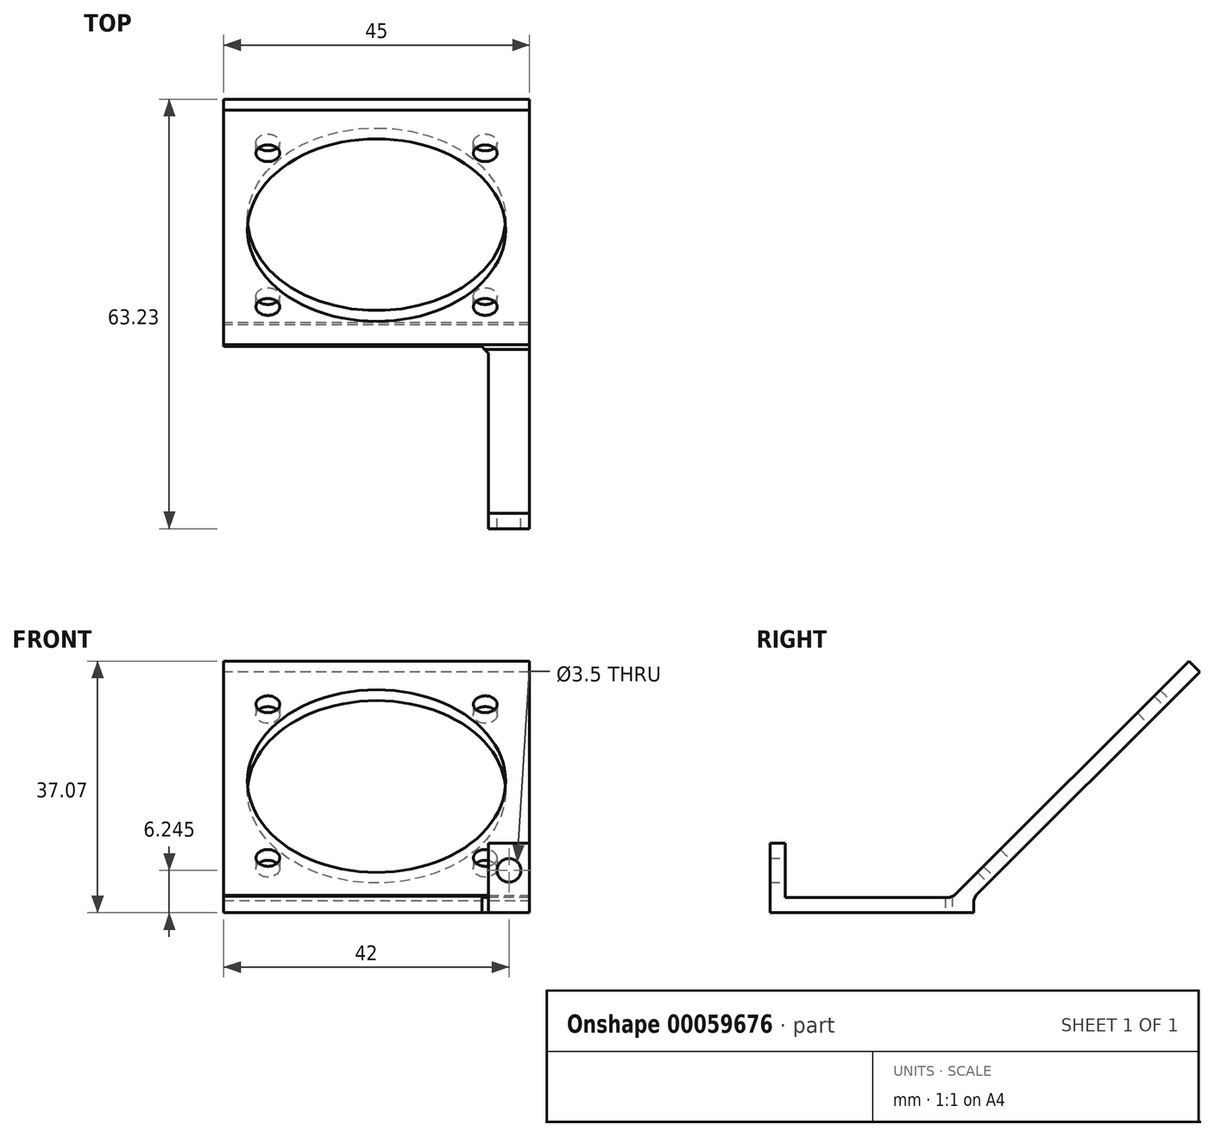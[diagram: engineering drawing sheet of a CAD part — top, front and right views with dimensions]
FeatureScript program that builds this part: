
annotation { "Feature Type Name" : "Feature", "Feature Type Description" : "" }
export const myFeature = defineFeature(function(context is Context, id is Id, definition is map)
    precondition{}
    {
        {
            var Q0;
            Q0=qCreatedBy(makeId("Right.planeOp"),FACE);
            var sketch = newSketch(context, id + "F0", { "sketchPlane" : qUnion([Q0])});
            skLineSegment(sketch, "E0.rect.bottom", {"start": v(15, 1.13) * mm, "end": v(-15, 1.12) * mm});
            skLineSegment(sketch, "E0.rect.top", {"start": v(15, -1.12) * mm, "end": v(-15, -1.13) * mm});
            skLineSegment(sketch, "E0.rect.left", {"start": v(15, 1.13) * mm, "end": v(15, -1.12) * mm});
            skLineSegment(sketch, "E0.rect.right", {"start": v(-15, 1.12) * mm, "end": v(-15, -1.13) * mm});
            skPoint(sketch, "E0.rect.middle", {"position": v(0, 0) * mm});
            skLineSegment(sketch, "E1", {"start": v(15, 1.13) * mm, "end": v(48.23, 34.36) * mm});
            skLineSegment(sketch, "E2.0", {"start": v(11.82, 1.13) * mm, "end": v(46.64, 35.95) * mm});
            skLineSegment(sketch, "E3", {"start": v(48.23, 34.36) * mm, "end": v(46.64, 35.95) * mm});
            skLineSegment(sketch, "E4.bottom", {"start": v(-15, 1.12) * mm, "end": v(-12.75, 1.12) * mm});
            skLineSegment(sketch, "E4.top", {"start": v(-15, 9.12) * mm, "end": v(-12.75, 9.12) * mm});
            skLineSegment(sketch, "E4.left", {"start": v(-15, 1.12) * mm, "end": v(-15, 9.12) * mm});
            skLineSegment(sketch, "E4.right", {"start": v(-12.75, 1.12) * mm, "end": v(-12.75, 9.12) * mm});
            skSolve(sketch);
        }
        {
            var Q0;
            Q0 = qSketchRegion(id + "F0", true);
            extrude(context, id + "F1", {"entities" : qUnion([Q0]), "depth" : 45 * mm});
        }
        {
            var Q0;
            Q0=makeQuery(id+"F1.opExtrude","SWEPT_FACE",FACE,{"disambiguationData":[OSD([sQuery(id+"F0.wireOp",EDGE,"E1")])]});
            var sketch = newSketch(context, id + "F2", { "sketchPlane" : qUnion([Q0])});
            skCircle(sketch, "E5", {"center": v(-22.5, 33.4) * mm, "radius": 19 * mm});
            skPoint(sketch, "E5.centerSnap0", {"position": v(-22.5, 58.4) * mm});
            skCircle(sketch, "E6", {"center": v(-6.5, 17.4) * mm, "radius": 1.75 * mm});
            skLineSegment(sketch, "E7", {"start": v(-22.5, 11.4) * mm, "end": v(-22.5, 58.4) * mm, "construction": true});
            skCircle(sketch, "E8.MirrorC", {"center": v(-38.5, 17.4) * mm, "radius": 1.75 * mm});
            skLineSegment(sketch, "E9", {"start": v(0, 33.4) * mm, "end": v(-45, 33.4) * mm, "construction": true});
            skCircle(sketch, "E10.MirrorC", {"center": v(-6.5, 49.4) * mm, "radius": 1.75 * mm});
            skCircle(sketch, "E11.MirrorC", {"center": v(-38.5, 49.4) * mm, "radius": 1.75 * mm});
            skSolve(sketch);
        }
        {
            var Q0;
            Q0 = qSketchRegion(id + "F2", true);
            extrude(context, id + "F3", {"entities" : qUnion([Q0]), "operationType" : NewBodyOperationType.REMOVE, "oppositeDirection" : true, "depth" : 3 * mm});
        }
        {
            var Q0;
            Q0=makeQuery(id+"F1.opExtrude","CAP_FACE",FACE,{"disambiguationData":[OSD([sQuery(id+"F0.wireOp",EDGE,"E0.rect.bottom"),sQuery(id+"F0.wireOp",EDGE,"E0.rect.top"),sQuery(id+"F0.wireOp",EDGE,"E0.rect.left"),sQuery(id+"F0.wireOp",EDGE,"E0.rect.right"),sQuery(id+"F0.wireOp",EDGE,"E1"),sQuery(id+"F0.wireOp",EDGE,"E2.0"),sQuery(id+"F0.wireOp",EDGE,"E3"),sQuery(id+"F0.wireOp",EDGE,"E4.top"),sQuery(id+"F0.wireOp",EDGE,"E4.left"),sQuery(id+"F0.wireOp",EDGE,"E4.right")])],"isStart":true});
            var sketch = newSketch(context, id + "F4", { "sketchPlane" : qUnion([Q0])});
            skLineSegment(sketch, "E12", {"start": v(-11.82, 1.13) * mm, "end": v(-11.82, -1.12) * mm});
            skSolve(sketch);
        }
        {
            var Q0;
            {var subQ1=sQuery(id+"F4.wireOp",EDGE,"E12");Q0=makeQuery(id+"F4.imprint","IMPRINT",FACE,{"disambiguationData":[TD([[makeQuery(id+"F4.imprint","IMPRINT",EDGE,{"derivedFrom":subQ1}),1.0]])]});}
            extrude(context, id + "F5", {"entities" : qUnion([Q0]), "operationType" : NewBodyOperationType.REMOVE, "oppositeDirection" : true, "depth" : 39 * mm});
        }
        {
            var Q0;
            Q0=makeQuery(id+"F1.opExtrude","SWEPT_FACE",FACE,{"disambiguationData":[OSD([sQuery(id+"F0.wireOp",EDGE,"E4.right")])]});
            var sketch = newSketch(context, id + "F6", { "sketchPlane" : qUnion([Q0])});
            skCircle(sketch, "E13", {"center": v(-42, 5.13) * mm, "radius": 1.75 * mm});
            skPoint(sketch, "E13.centerSnap0", {"position": v(-45, 5.13) * mm});
            skPoint(sketch, "E13.centerSnap1", {"position": v(-42, 1.13) * mm});
            skSolve(sketch);
        }
        {
            var Q0;
            Q0 = qSketchRegion(id + "F6", true);
            extrude(context, id + "F7", {"entities" : qUnion([Q0]), "operationType" : NewBodyOperationType.REMOVE, "endBound" : BoundingType.THROUGH_ALL, "oppositeDirection" : true, "depth" : 25 * mm});
        }
        {
            var Q0;
            Q0=makeQuery(id+"F1.opExtrude","SWEPT_EDGE",EDGE,{"disambiguationData":[OSD([sQuery(id+"F0.wireOp",EDGE,"E0.rect.bottom"),sQuery(id+"F0.wireOp",EDGE,"E0.rect.left"),sQuery(id+"F0.wireOp",EDGE,"E1")])]});
            var Q1;
            Q1=makeQuery(id+"F5.boolean.opBoolean","SPLIT",EDGE,{"derivedFrom":makeQuery(id+"F1.opExtrude","SWEPT_EDGE",EDGE,{"disambiguationData":[OSD([sQuery(id+"F0.wireOp",EDGE,"E0.rect.bottom"),sQuery(id+"F0.wireOp",EDGE,"E2.0")])]})});
            var Q2;
            Q2=makeQuery(id+"F5.boolean.opBoolean","COPY",EDGE,{"derivedFrom":makeQuery(id+"F5.opExtrude","CAP_EDGE",EDGE,{"disambiguationData":[OSD([sQuery(id+"F4.wireOp",EDGE,"E12")])],"isStart":false})});
            chamfer(context, id + "F8", {"entities" : qUnion([Q0, Q1, Q2]), "width" : 1 * mm, "tangentPropagation" : true});
        }
    });
